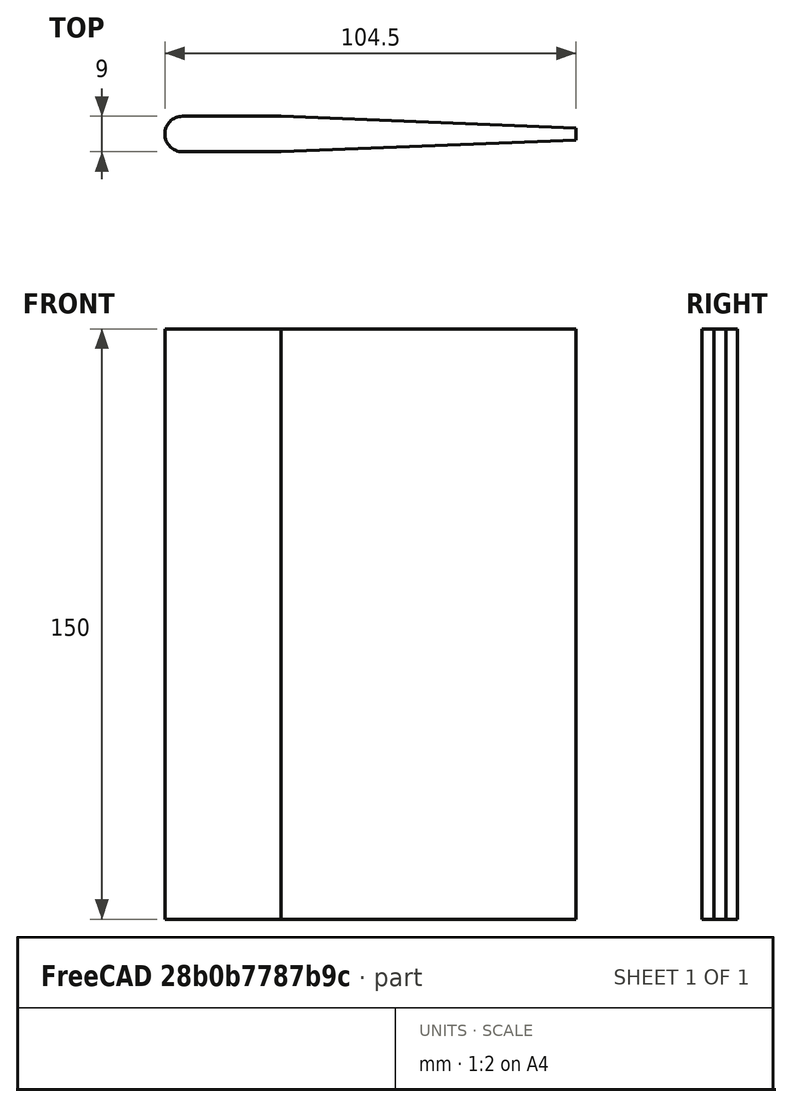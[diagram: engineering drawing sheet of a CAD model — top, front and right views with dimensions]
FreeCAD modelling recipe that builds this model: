
FCSTD DOCUMENT  (FreeCAD 0.16R6706 (Git))
Label: Aile_20170119
License: All rights reserved
LicenseURL: http://en.wikipedia.org/wiki/All_rights_reserved
objects: Sketcher::SketchObject×1, PartDesign::Pad×1
note: 3 computed .brp shape members not serialized (recipe doc carries the construction recipe); baked Part::Feature solids carry a one-line shape summary decoded from their .brp

FEATURE [Sketcher::SketchObject] Sketch
  sketch-geometry (6):
    g0: LineSegment StartX=-18.6614 StartY=4.5 StartZ=0 EndX=6.33862 EndY=4.5 EndZ=0
    g1: LineSegment StartX=-18.6614 StartY=-4.5 StartZ=0 EndX=6.33862 EndY=-4.5 EndZ=0
    g2: LineSegment StartX=6.33862 StartY=4.5 StartZ=0 EndX=81.3386 EndY=1.5 EndZ=0
    g3: LineSegment StartX=6.33862 StartY=-4.5 StartZ=0 EndX=81.3386 EndY=-1.5 EndZ=0
    g4: ArcOfCircle CenterX=-18.6614 CenterY=0 CenterZ=0 NormalX=0 NormalY=0 NormalZ=1 Radius=4.5 StartAngle=1.5708 EndAngle=4.71239
    g5: LineSegment StartX=81.3386 StartY=1.5 StartZ=0 EndX=81.3386 EndY=-1.5 EndZ=0
  constraints (16):
    c: Coincident(g4,g0)
    c: Coincident(g1,g4)
    c: Radius(g4) = 4.5
    c: Parallel(g0,g1)
    c: Coincident(g0,g2)
    c: Coincident(g3,g1)
    c: Coincident(g2,g5)
    c: Coincident(g3,g5)
    c: Parallel(g0,g-1)
    c: Symmetric(g3,g2,g-1)
    c: Distance(g2,g3) = 3
    c: Symmetric(g0,g1,g-1)
    c: Symmetric(g0,g1,g-1)
    c: Distance(g0) = 25
    c: DistanceX(g0,g2) = 75
    c: DistanceY(g1,g0) = 9
FEATURE [PartDesign::Pad] Pad
  Length = 150
  Length2 = 100
  Sketch = -> Sketch
  Type = 0
